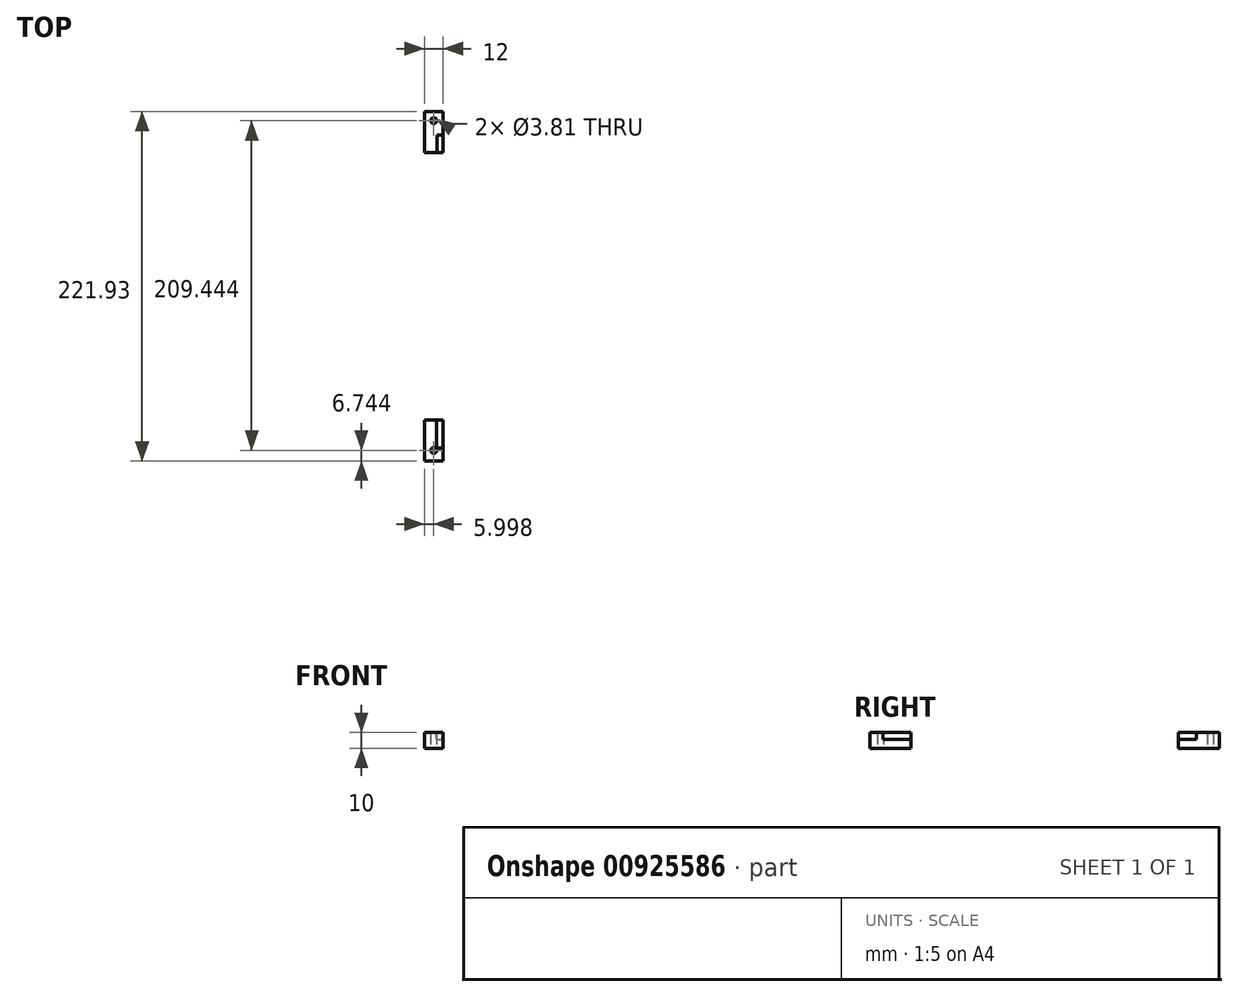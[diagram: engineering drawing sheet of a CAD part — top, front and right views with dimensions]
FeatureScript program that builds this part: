
annotation { "Feature Type Name" : "Feature", "Feature Type Description" : "" }
export const myFeature = defineFeature(function(context is Context, id is Id, definition is map)
    precondition{}
    {
        {
            var Q0;
            Q0=qCreatedBy(makeId("Top.planeOp"),FACE);
            var sketch = newSketch(context, id + "F0", { "sketchPlane" : qUnion([Q0])});
            skCircle(sketch, "E0.0", {"center": v(-150.18, 163.07) * mm, "radius": 1.9 * mm});
            skCircle(sketch, "E1.0", {"center": v(100.96, -46.38) * mm, "radius": 1.9 * mm, "construction": true});
            skCircle(sketch, "E2.0", {"center": v(-150.18, -46.38) * mm, "radius": 1.9 * mm});
            skLineSegment(sketch, "E3.0", {"start": v(-144.34, -38.16) * mm, "end": v(-144.34, -42.33) * mm, "construction": true});
            skLineSegment(sketch, "E4.0", {"start": v(-146.73, -38.16) * mm, "end": v(-144.34, -38.16) * mm, "construction": true});
            skLineSegment(sketch, "E5.0", {"start": v(-146.73, -38.16) * mm, "end": v(-146.73, 151.27) * mm, "construction": true});
            skLineSegment(sketch, "E6.0", {"start": v(-144.34, -42.33) * mm, "end": v(95.12, -42.33) * mm, "construction": true});
            skLineSegment(sketch, "E7.0", {"start": v(95.12, -38.16) * mm, "end": v(95.12, -42.33) * mm, "construction": true});
            skLineSegment(sketch, "E8.0", {"start": v(95.12, -38.16) * mm, "end": v(97.5, -38.16) * mm, "construction": true});
            skLineSegment(sketch, "E9.0", {"start": v(97.5, -38.16) * mm, "end": v(97.5, 151.27) * mm, "construction": true});
            skLineSegment(sketch, "E10.0", {"start": v(-146.73, 151.27) * mm, "end": v(97.5, 151.27) * mm, "construction": true});
            skCircle(sketch, "E11.0", {"center": v(100.96, 163.07) * mm, "radius": 1.9 * mm, "construction": true});
            skLineSegment(sketch, "E11.1", {"start": v(-203.32, 169.81) * mm, "end": v(154.1, 169.81) * mm, "construction": true});
            skLineSegment(sketch, "E12.bottom", {"start": v(-156.18, 168.81) * mm, "end": v(-144.18, 168.81) * mm});
            skLineSegment(sketch, "E12.top", {"start": v(-156.18, 142.81) * mm, "end": v(-144.18, 142.81) * mm});
            skLineSegment(sketch, "E12.left", {"start": v(-156.18, 168.81) * mm, "end": v(-156.18, 142.81) * mm});
            skLineSegment(sketch, "E12.right", {"start": v(-144.18, 168.81) * mm, "end": v(-144.18, 142.81) * mm});
            skLineSegment(sketch, "E13.bottom", {"start": v(-156.18, -27.12) * mm, "end": v(-144.18, -27.12) * mm});
            skLineSegment(sketch, "E13.top", {"start": v(-156.18, -53.12) * mm, "end": v(-144.18, -53.12) * mm});
            skLineSegment(sketch, "E13.left", {"start": v(-156.18, -27.12) * mm, "end": v(-156.18, -53.12) * mm});
            skLineSegment(sketch, "E13.right", {"start": v(-144.18, -27.12) * mm, "end": v(-144.18, -53.12) * mm});
            skSolve(sketch);
        }
        {
            var Q0;
            Q0 = qSketchRegion(id + "F0", true);
            extrude(context, id + "F1", {"entities" : qUnion([Q0]), "depth" : 10 * mm, "offsetDistance" : 25 * mm});
        }
        {
            var Q0;
            Q0=makeQuery(id+"F1.opExtrude","CAP_FACE",FACE,{"disambiguationData":[OSD([sQuery(id+"F0.wireOp",EDGE,"E0.0"),sQuery(id+"F0.wireOp",EDGE,"E12.bottom"),sQuery(id+"F0.wireOp",EDGE,"E12.top"),sQuery(id+"F0.wireOp",EDGE,"E12.left"),sQuery(id+"F0.wireOp",EDGE,"E12.right")])],"isStart":false});
            var sketch = newSketch(context, id + "F2", { "sketchPlane" : qUnion([Q0])});
            skLineSegment(sketch, "E14.bottom", {"start": v(-146.73, 151.27) * mm, "end": v(-144.18, 151.27) * mm, "construction": true});
            skLineSegment(sketch, "E14.top", {"start": v(-146.73, 142.81) * mm, "end": v(-144.18, 142.81) * mm, "construction": true});
            skLineSegment(sketch, "E14.left", {"start": v(-146.73, 151.27) * mm, "end": v(-146.73, 142.81) * mm, "construction": true});
            skLineSegment(sketch, "E14.right", {"start": v(-144.18, 151.27) * mm, "end": v(-144.18, 142.81) * mm, "construction": true});
            skLineSegment(sketch, "E15.bottom", {"start": v(-146.73, -26.94) * mm, "end": v(-143.43, -26.94) * mm, "construction": true});
            skLineSegment(sketch, "E15.top", {"start": v(-146.73, -42.33) * mm, "end": v(-143.43, -42.33) * mm, "construction": true});
            skLineSegment(sketch, "E15.left", {"start": v(-146.73, -26.94) * mm, "end": v(-146.73, -42.33) * mm, "construction": true});
            skLineSegment(sketch, "E15.right", {"start": v(-143.43, -26.94) * mm, "end": v(-143.43, -42.33) * mm, "construction": true});
            skLineSegment(sketch, "E16.0", {"start": v(-147.73, -25.94) * mm, "end": v(-142.43, -25.94) * mm});
            skLineSegment(sketch, "E16.3", {"start": v(-142.43, -25.94) * mm, "end": v(-142.43, -43.33) * mm});
            skLineSegment(sketch, "E17.0", {"start": v(-148.1, 153.98) * mm, "end": v(-143.18, 153.98) * mm});
            skLineSegment(sketch, "E17.1", {"start": v(-148.1, 153.98) * mm, "end": v(-148.1, 141.81) * mm});
            skLineSegment(sketch, "E17.2", {"start": v(-148.1, 141.81) * mm, "end": v(-143.18, 141.81) * mm});
            skLineSegment(sketch, "E17.3", {"start": v(-143.18, 153.98) * mm, "end": v(-143.18, 141.81) * mm});
            skLineSegment(sketch, "E18", {"start": v(-147.73, -25.94) * mm, "end": v(-148.27, -25.94) * mm});
            skLineSegment(sketch, "E19", {"start": v(-148.27, -25.94) * mm, "end": v(-148.27, -43.77) * mm});
            skLineSegment(sketch, "E20", {"start": v(-148.27, -43.77) * mm, "end": v(-142.43, -43.77) * mm});
            skLineSegment(sketch, "E21", {"start": v(-142.43, -43.77) * mm, "end": v(-142.43, -43.33) * mm});
            skSolve(sketch);
        }
        {
            var Q0;
            {var subQ1=sQuery(id+"F2.wireOp",EDGE,"E17.2");Q0=makeQuery(id+"F2.imprint","IMPRINT",FACE,{"disambiguationData":[TD([[makeQuery(id+"F2.imprint","IMPRINT",EDGE,{"derivedFrom":subQ1}),1.0]])]});}
            var Q1;
            {var subQ0=sQuery(id+"F2.wireOp",EDGE,"E17.1");var subQ1=sQuery(id+"F2.wireOp",EDGE,"E17.0");var subQ2=makeQuery(id+"F2.imprint","INTERSECT",VERTEX,{"derivedFrom":[subQ1,subQ0]});Q1=makeQuery(id+"F2.imprint","IMPRINT",FACE,{"disambiguationData":[TD([[makeQuery(id+"F2.imprint","IMPRINT",EDGE,{"disambiguationData":[TD([[subQ2,-1.0]])],"derivedFrom":subQ1}),-1.0]])]});}
            var Q2;
            Q2=sQuery(id+"F2.wireOp",EDGE,"E14.left");
            var Q3;
            Q3=sQuery(id+"F2.wireOp",EDGE,"E14.bottom");
            var Q4;
            Q4=sQuery(id+"F2.wireOp",EDGE,"E14.right");
            var Q5;
            Q5=sQuery(id+"F2.wireOp",EDGE,"E14.top");
            extrude(context, id + "F3", {"entities" : qUnion([Q0, Q1]), "operationType" : NewBodyOperationType.REMOVE, "surfaceEntities" : qUnion([Q2, Q3, Q4, Q5]), "oppositeDirection" : true, "depth" : 4.3 * mm, "offsetDistance" : 25 * mm});
        }
        {
            var Q0;
            Q0=makeQuery(id+"F1.opExtrude","CAP_FACE",FACE,{"disambiguationData":[OSD([sQuery(id+"F0.wireOp",EDGE,"E2.0"),sQuery(id+"F0.wireOp",EDGE,"E13.bottom"),sQuery(id+"F0.wireOp",EDGE,"E13.top"),sQuery(id+"F0.wireOp",EDGE,"E13.left"),sQuery(id+"F0.wireOp",EDGE,"E13.right")])],"isStart":false});
            var sketch = newSketch(context, id + "F4", { "sketchPlane" : qUnion([Q0])});
            skLineSegment(sketch, "E22.0", {"start": v(-147.73, -25.94) * mm, "end": v(-142.43, -25.94) * mm});
            skLineSegment(sketch, "E22.3", {"start": v(-142.43, -25.94) * mm, "end": v(-142.43, -43.33) * mm});
            skLineSegment(sketch, "E23", {"start": v(-142.43, -44.9) * mm, "end": v(-142.43, -43.33) * mm});
            skLineSegment(sketch, "E24", {"start": v(-142.43, -44.9) * mm, "end": v(-147.73, -44.9) * mm});
            skPoint(sketch, "E22.2.start.orphan", {"position": v(-147.73, -43.33) * mm});
            skLineSegment(sketch, "E25", {"start": v(-147.73, -25.94) * mm, "end": v(-148.3, -25.94) * mm});
            skLineSegment(sketch, "E26", {"start": v(-148.3, -25.94) * mm, "end": v(-148.3, -44.9) * mm});
            skLineSegment(sketch, "E27", {"start": v(-148.3, -44.9) * mm, "end": v(-147.73, -44.9) * mm});
            skPoint(sketch, "E22.1.start.orphan", {"position": v(-147.73, -25.94) * mm});
            skSolve(sketch);
        }
        {
            var Q0;
            Q0 = qSketchRegion(id + "F4", true);
            extrude(context, id + "F5", {"entities" : qUnion([Q0]), "operationType" : NewBodyOperationType.REMOVE, "oppositeDirection" : true, "depth" : 4.2 * mm, "offsetDistance" : 25 * mm});
        }
    });
